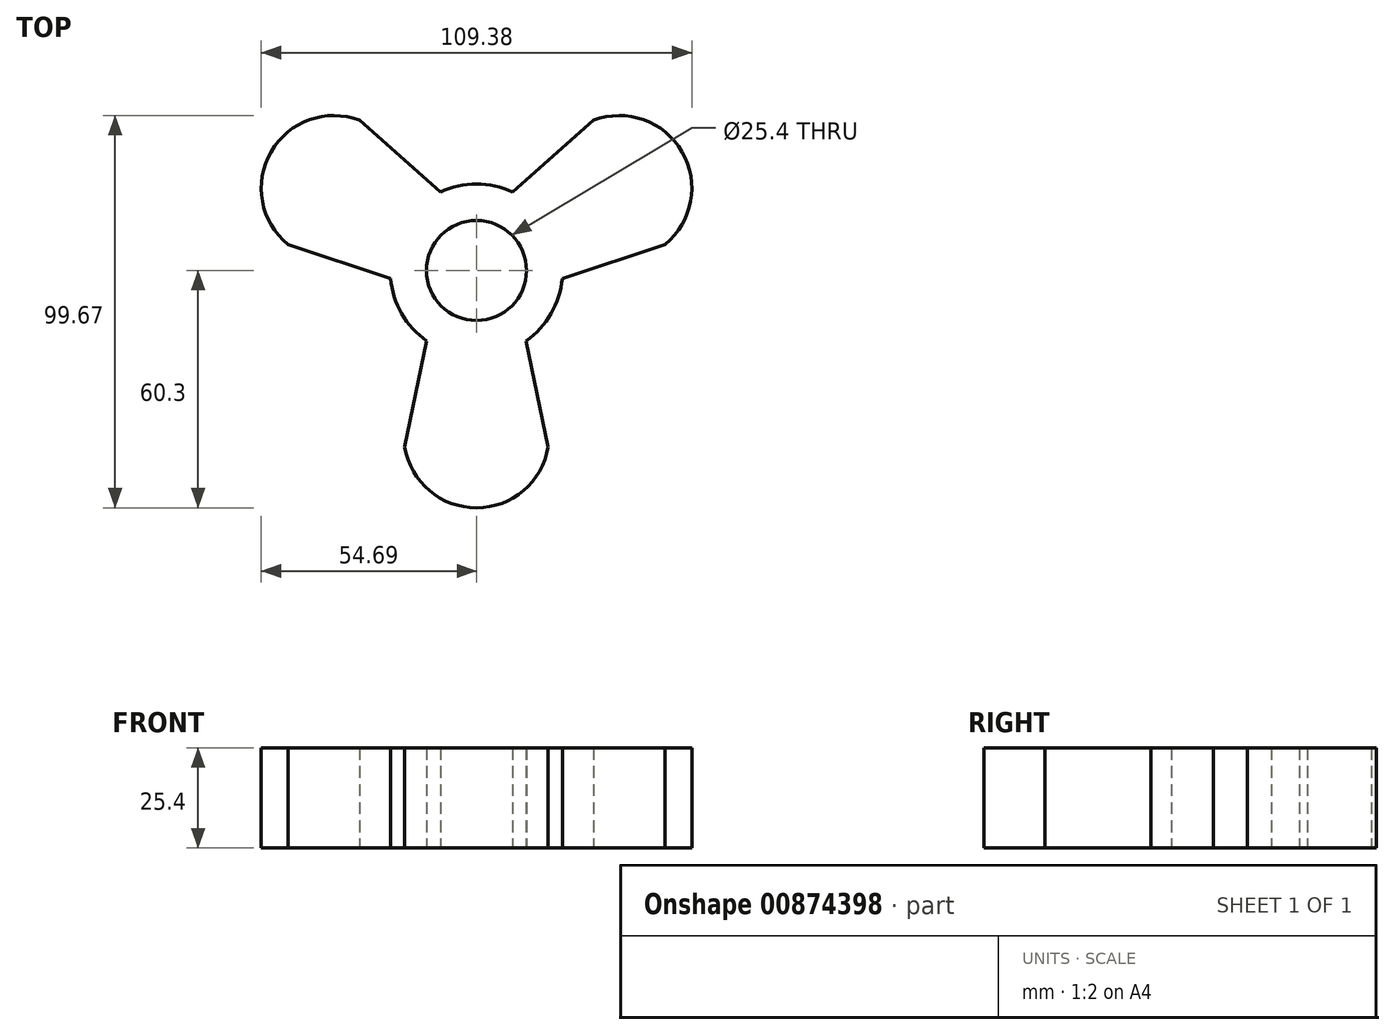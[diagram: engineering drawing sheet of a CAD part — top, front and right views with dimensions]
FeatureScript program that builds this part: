
annotation { "Feature Type Name" : "Feature", "Feature Type Description" : "" }
export const myFeature = defineFeature(function(context is Context, id is Id, definition is map)
    precondition{}
    {
        {
            var Q0;
            Q0=qCreatedBy(makeId("Top.planeOp"),FACE);
            var sketch = newSketch(context, id + "F0", { "sketchPlane" : qUnion([Q0])});
            skCircle(sketch, "E0", {"center": v(0, 0) * mm, "radius": 12.7 * mm});
            skLineSegment(sketch, "E1", {"start": v(-12.64, -17.9) * mm, "end": v(-18.2, -44.82) * mm});
            skLineSegment(sketch, "E2", {"start": v(12.64, -17.9) * mm, "end": v(18.2, -44.82) * mm});
            skArc(sketch, "E3", {"start": v(-18.2, -44.82) * mm, "mid": v(0, -60.3) * mm, "end": v(18.2, -44.82) * mm});
            skLineSegment(sketch, "E4", {"start": v(0, 0) * mm, "end": v(69.07, 39.88) * mm, "construction": true});
            skLineSegment(sketch, "E5.MirrorCS", {"start": v(-21.82, -2) * mm, "end": v(-47.91, 6.64) * mm});
            skArc(sketch, "E6.MirrorCS", {"start": v(-47.91, 6.64) * mm, "mid": v(-52.22, 30.15) * mm, "end": v(-29.71, 38.17) * mm});
            skLineSegment(sketch, "E7.MirrorCS", {"start": v(-9.17, 19.9) * mm, "end": v(-29.71, 38.17) * mm});
            skLineSegment(sketch, "E8", {"start": v(0, 0) * mm, "end": v(-36.25, 20.93) * mm, "construction": true});
            skLineSegment(sketch, "E9.MirrorCS", {"start": v(9.17, 19.9) * mm, "end": v(29.71, 38.17) * mm});
            skArc(sketch, "E10.MirrorCS", {"start": v(29.71, 38.17) * mm, "mid": v(52.22, 30.15) * mm, "end": v(47.91, 6.64) * mm});
            skLineSegment(sketch, "E11.MirrorCS", {"start": v(21.82, -2) * mm, "end": v(47.91, 6.64) * mm});
            skArc(sketch, "E12", {"start": v(-21.82, -2) * mm, "mid": v(-19, -10.97) * mm, "end": v(-12.64, -17.9) * mm});
            skArc(sketch, "E13", {"start": v(12.64, -17.9) * mm, "mid": v(18.94, -10.94) * mm, "end": v(21.82, -2) * mm});
            skArc(sketch, "E14", {"start": v(9.17, 19.9) * mm, "mid": v(0, 21.97) * mm, "end": v(-9.17, 19.9) * mm});
            skSolve(sketch);
        }
        {
            var Q0;
            Q0 = qSketchRegion(id + "F0", true);
            extrude(context, id + "F1", {"entities" : qUnion([Q0]), "depth" : 25.4 * mm, "offsetDistance" : 25.4 * mm});
        }
    });
